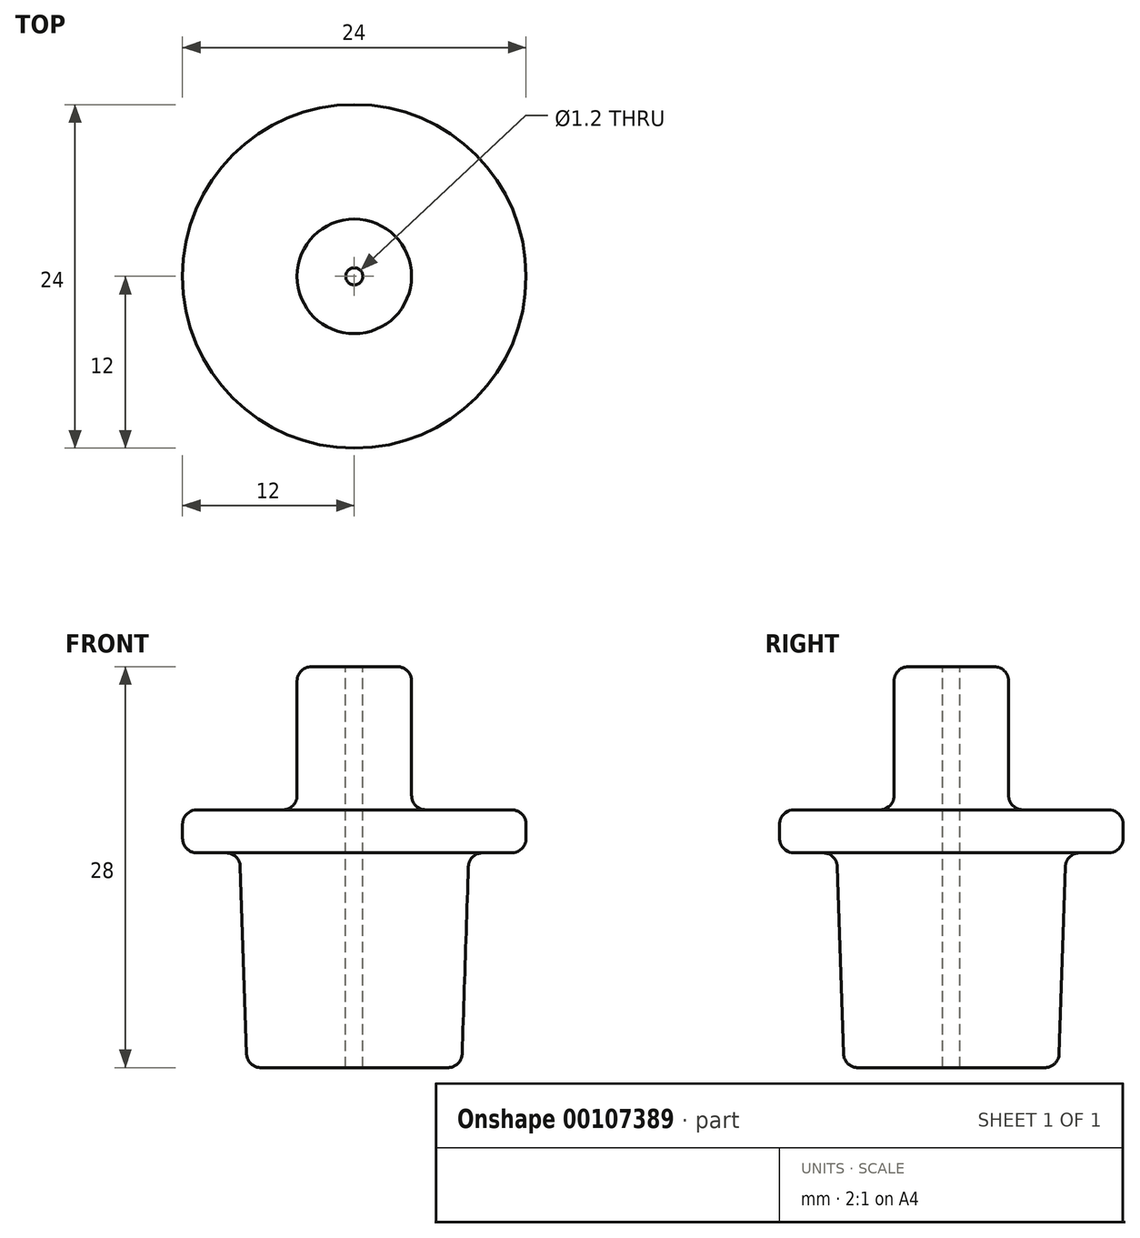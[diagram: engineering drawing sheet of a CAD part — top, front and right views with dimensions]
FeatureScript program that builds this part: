
annotation { "Feature Type Name" : "Feature", "Feature Type Description" : "" }
export const myFeature = defineFeature(function(context is Context, id is Id, definition is map)
    precondition{}
    {
        {
            var Q0;
            Q0=qCreatedBy(makeId("Front.planeOp"),FACE);
            var sketch = newSketch(context, id + "F0", { "sketchPlane" : qUnion([Q0])});
            skLineSegment(sketch, "E0", {"start": v(0, 10.35) * mm, "end": v(0, -9.76) * mm, "construction": true});
            skLineSegment(sketch, "E1", {"start": v(0.6, 16.68) * mm, "end": v(0.6, -11.32) * mm});
            skLineSegment(sketch, "E2", {"start": v(0.6, 16.68) * mm, "end": v(4, 16.68) * mm});
            skLineSegment(sketch, "E3", {"start": v(4, 16.68) * mm, "end": v(4, 6.68) * mm});
            skLineSegment(sketch, "E4", {"start": v(4, 6.68) * mm, "end": v(12, 6.68) * mm});
            skLineSegment(sketch, "E5", {"start": v(12, 6.68) * mm, "end": v(12, 3.68) * mm});
            skLineSegment(sketch, "E6", {"start": v(12, 3.68) * mm, "end": v(8, 3.68) * mm});
            skLineSegment(sketch, "E7", {"start": v(8, 3.68) * mm, "end": v(7.5, -11.32) * mm});
            skLineSegment(sketch, "E8", {"start": v(7.5, -11.32) * mm, "end": v(0.6, -11.32) * mm});
            skSolve(sketch);
        }
        {
            var Q0;
            Q0=makeQuery(id+"F0.imprint","IMPRINT",FACE,{"disambiguationData":[TD([[makeQuery(id+"F0.imprint","IMPRINT",EDGE,{"derivedFrom":sQuery(id+"F0.wireOp",EDGE,"E1")}),1.0]])]});
            var Q1;
            Q1=makeQuery(id+"F0.imprint","IMPRINT",FACE,{"disambiguationData":[TD([[makeQuery(id+"F0.imprint","IMPRINT",EDGE,{"derivedFrom":sQuery(id+"F0.wireOp",EDGE,"E1")}),1.0]])]});
            var Q2;
            Q2=sQuery(id+"F0.wireOp",EDGE,"E0");
            revolve(context, id + "F1", {"entities" : qUnion([Q0, Q1]), "axis" : qUnion([Q2]), "revolveType" : RevolveType.FULL});
        }
        {
            var Q0;
            Q0=makeQuery(id+"F1.opRevolve","SWEPT_EDGE",EDGE,{"disambiguationData":[OSD([sQuery(id+"F0.wireOp",EDGE,"E7"),sQuery(id+"F0.wireOp",EDGE,"E8")])]});
            var Q1;
            Q1=makeQuery(id+"F1.opRevolve","SWEPT_EDGE",EDGE,{"disambiguationData":[OSD([sQuery(id+"F0.wireOp",EDGE,"E6"),sQuery(id+"F0.wireOp",EDGE,"E7")])]});
            var Q2;
            Q2=makeQuery(id+"F1.opRevolve","SWEPT_EDGE",EDGE,{"disambiguationData":[OSD([sQuery(id+"F0.wireOp",EDGE,"E5"),sQuery(id+"F0.wireOp",EDGE,"E6")])]});
            var Q3;
            Q3=makeQuery(id+"F1.opRevolve","SWEPT_EDGE",EDGE,{"disambiguationData":[OSD([sQuery(id+"F0.wireOp",EDGE,"E4"),sQuery(id+"F0.wireOp",EDGE,"E5")])]});
            var Q4;
            Q4=makeQuery(id+"F1.opRevolve","SWEPT_EDGE",EDGE,{"disambiguationData":[OSD([sQuery(id+"F0.wireOp",EDGE,"E2"),sQuery(id+"F0.wireOp",EDGE,"E3")])]});
            var Q5;
            Q5=makeQuery(id+"F1.opRevolve","SWEPT_EDGE",EDGE,{"disambiguationData":[OSD([sQuery(id+"F0.wireOp",EDGE,"E3"),sQuery(id+"F0.wireOp",EDGE,"E4")])]});
            fillet(context, id + "F2", {"entities" : qUnion([Q0, Q1, Q2, Q3, Q4, Q5]), "radius" : 1 * mm, "tangentPropagation" : true, "allowEdgeOverflow" : false});
        }
    });
